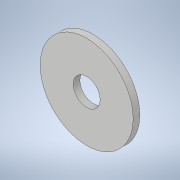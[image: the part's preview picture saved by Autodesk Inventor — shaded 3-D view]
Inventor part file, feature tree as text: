
AUTODESK INVENTOR PART (.ipt)
format: ipt  version: 2020.2 (Build 242310000, 310)  size: 95,744 bytes
history: native  units: mm
features: extrude x1, sketch x1
ambient origin geometry x8: Origin, YZ Plane, XZ Plane, XY Plane, X Axis, Y Axis, Z Axis, Center Point
bodies: Solid1 (feature_tree)
feature tree (2):
  extrude  "Extrusion1"  Depth=1.0mm
  sketch  "Sketch1"  dims[d0=14.0mm d1=4.05mm d2=1.0mm d3=0.0mm]
